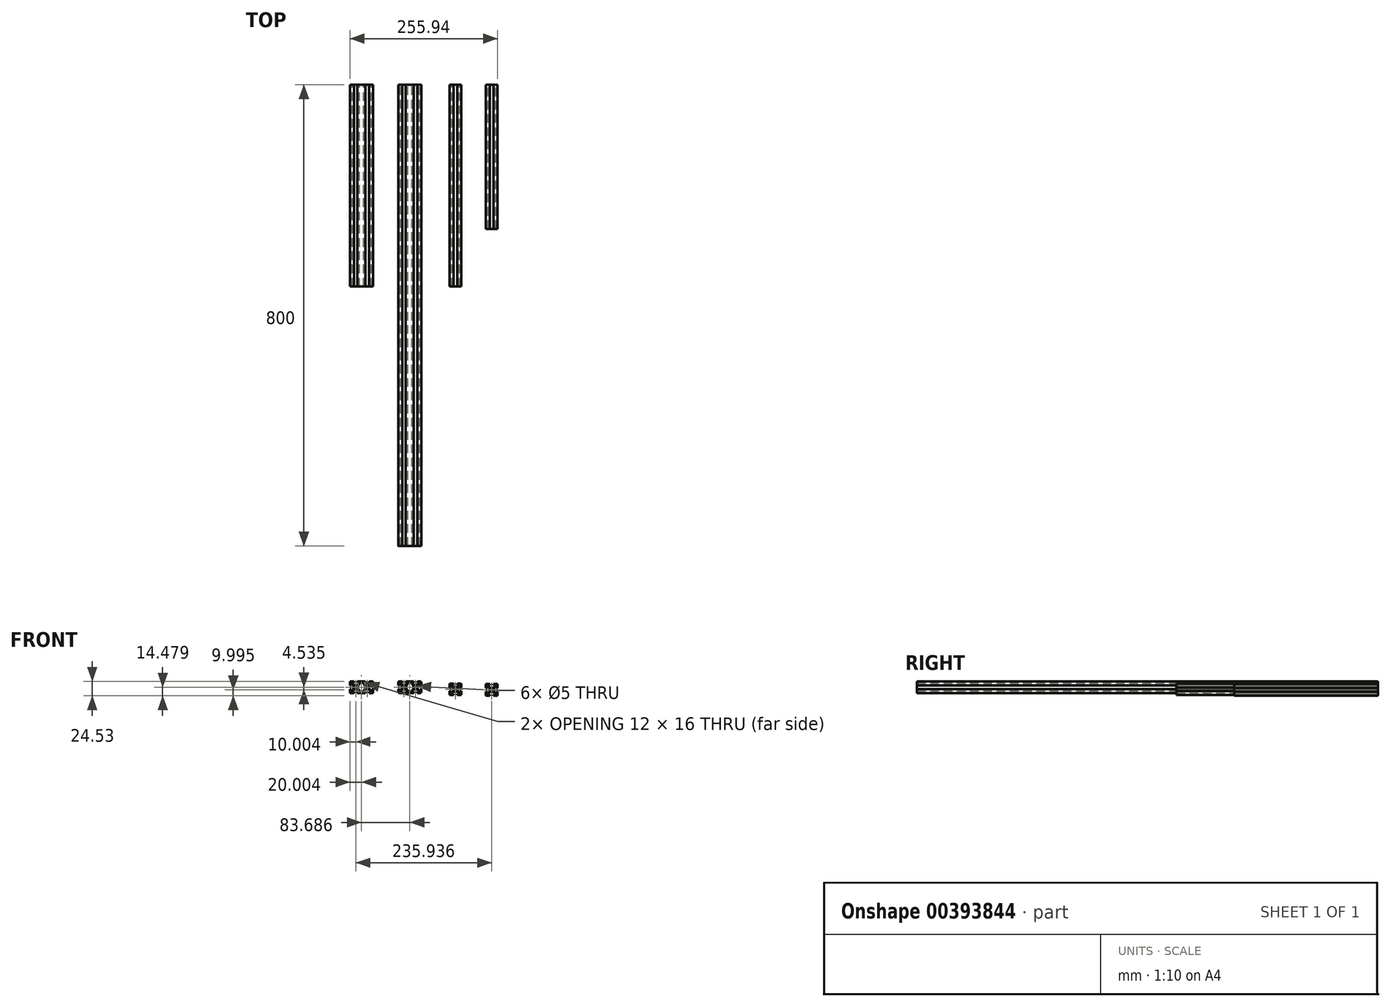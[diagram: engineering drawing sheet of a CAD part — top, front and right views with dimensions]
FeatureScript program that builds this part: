
annotation { "Feature Type Name" : "Feature", "Feature Type Description" : "" }
export const myFeature = defineFeature(function(context is Context, id is Id, definition is map)
    precondition{}
    {
        {
            var Q0;
            Q0=qCreatedBy(makeId("Front.planeOp"),FACE);
            var sketch = newSketch(context, id + "F0", { "sketchPlane" : qUnion([Q0])});
            skLineSegment(sketch, "E0.bottom", {"start": v(-20, 10) * mm, "end": v(-13, 10) * mm});
            skLineSegment(sketch, "E0.top", {"start": v(-20, -10) * mm, "end": v(-13, -10) * mm});
            skLineSegment(sketch, "E0.left", {"start": v(-20, 10) * mm, "end": v(-20, 3) * mm});
            skPoint(sketch, "E1.endSnap0", {"position": v(0, -10) * mm});
            skLineSegment(sketch, "E2", {"start": v(-26.6, 0) * mm, "end": v(32.73, 0) * mm, "construction": true});
            skCircle(sketch, "E3", {"center": v(10, 0) * mm, "radius": 2.5 * mm});
            skCircle(sketch, "E4", {"center": v(-10, 0) * mm, "radius": 2.5 * mm});
            skLineSegment(sketch, "E5", {"start": v(4.5, 8) * mm, "end": v(7, 8) * mm});
            skLineSegment(sketch, "E6", {"start": v(15.5, 8) * mm, "end": v(15.5, 6.5) * mm});
            skLineSegment(sketch, "E7", {"start": v(15.5, 6.5) * mm, "end": v(13, 4) * mm});
            skLineSegment(sketch, "E8", {"start": v(13, 4) * mm, "end": v(7, 4) * mm});
            skLineSegment(sketch, "E9", {"start": v(7, 4) * mm, "end": v(4.5, 6.5) * mm});
            skLineSegment(sketch, "E10", {"start": v(4.5, 6.5) * mm, "end": v(4.5, 8) * mm});
            skLineSegment(sketch, "E11", {"start": v(0, 29.93) * mm, "end": v(0, -23.02) * mm, "construction": true});
            skLineSegment(sketch, "E12", {"start": v(7, 8) * mm, "end": v(7, 10) * mm});
            skLineSegment(sketch, "E13", {"start": v(13, 8) * mm, "end": v(13, 10) * mm});
            skLineSegment(sketch, "E14.trimOffspring", {"start": v(13, 8) * mm, "end": v(15.5, 8) * mm});
            skLineSegment(sketch, "E15.trimOffspring", {"start": v(13, 10) * mm, "end": v(20, 10) * mm});
            skLineSegment(sketch, "E16.1.3", {"start": v(6, -3) * mm, "end": v(3.5, -5.5) * mm});
            skLineSegment(sketch, "E16.1.4", {"start": v(6, 3) * mm, "end": v(6, -3) * mm});
            skLineSegment(sketch, "E16.1.5", {"start": v(3.5, 5.5) * mm, "end": v(6, 3) * mm});
            skLineSegment(sketch, "E16.2.0", {"start": v(13, -8) * mm, "end": v(13, -10) * mm});
            skLineSegment(sketch, "E16.2.1", {"start": v(15.5, -8) * mm, "end": v(13, -8) * mm});
            skLineSegment(sketch, "E16.2.2", {"start": v(15.5, -6.5) * mm, "end": v(15.5, -8) * mm});
            skLineSegment(sketch, "E16.2.3", {"start": v(13, -4) * mm, "end": v(15.5, -6.5) * mm});
            skLineSegment(sketch, "E16.2.4", {"start": v(7, -4) * mm, "end": v(13, -4) * mm});
            skLineSegment(sketch, "E16.2.5", {"start": v(4.5, -6.5) * mm, "end": v(7, -4) * mm});
            skLineSegment(sketch, "E16.2.6", {"start": v(7, -8) * mm, "end": v(7, -10) * mm});
            skLineSegment(sketch, "E16.2.7", {"start": v(7, -8) * mm, "end": v(4.5, -8) * mm});
            skLineSegment(sketch, "E16.2.8", {"start": v(4.5, -8) * mm, "end": v(4.5, -6.5) * mm});
            skLineSegment(sketch, "E16.3.0", {"start": v(18, 3) * mm, "end": v(20, 3) * mm});
            skLineSegment(sketch, "E16.3.1", {"start": v(18, 5.5) * mm, "end": v(18, 3) * mm});
            skLineSegment(sketch, "E16.3.2", {"start": v(16.5, 5.5) * mm, "end": v(18, 5.5) * mm});
            skLineSegment(sketch, "E16.3.3", {"start": v(14, 3) * mm, "end": v(16.5, 5.5) * mm});
            skLineSegment(sketch, "E16.3.4", {"start": v(14, -3) * mm, "end": v(14, 3) * mm});
            skLineSegment(sketch, "E16.3.5", {"start": v(16.5, -5.5) * mm, "end": v(14, -3) * mm});
            skLineSegment(sketch, "E16.3.6", {"start": v(18, -3) * mm, "end": v(20, -3) * mm});
            skLineSegment(sketch, "E16.3.7", {"start": v(18, -3) * mm, "end": v(18, -5.5) * mm});
            skLineSegment(sketch, "E16.3.8", {"start": v(18, -5.5) * mm, "end": v(16.5, -5.5) * mm});
            skLineSegment(sketch, "E17.MirrorCS", {"start": v(-4.5, -8) * mm, "end": v(-4.5, -6.5) * mm});
            skLineSegment(sketch, "E18.MirrorCS", {"start": v(-4.5, -6.5) * mm, "end": v(-7, -4) * mm});
            skLineSegment(sketch, "E19.MirrorCS", {"start": v(-7, -4) * mm, "end": v(-13, -4) * mm});
            skLineSegment(sketch, "E20.MirrorCS", {"start": v(-7, -8) * mm, "end": v(-4.5, -8) * mm});
            skLineSegment(sketch, "E21.MirrorCS", {"start": v(-7, -8) * mm, "end": v(-7, -10) * mm});
            skLineSegment(sketch, "E22.MirrorCS", {"start": v(-13, -8) * mm, "end": v(-13, -10) * mm});
            skLineSegment(sketch, "E23.MirrorCS", {"start": v(-15.5, -8) * mm, "end": v(-13, -8) * mm});
            skLineSegment(sketch, "E24.MirrorCS", {"start": v(-15.5, -6.5) * mm, "end": v(-15.5, -8) * mm});
            skLineSegment(sketch, "E25.MirrorCS", {"start": v(-13, -4) * mm, "end": v(-15.5, -6.5) * mm});
            skLineSegment(sketch, "E26.MirrorCS", {"start": v(-14, -3) * mm, "end": v(-14, 3) * mm});
            skLineSegment(sketch, "E27.MirrorCS", {"start": v(-16.5, -5.5) * mm, "end": v(-14, -3) * mm});
            skLineSegment(sketch, "E28.MirrorCS", {"start": v(-18, -5.5) * mm, "end": v(-16.5, -5.5) * mm});
            skLineSegment(sketch, "E29.MirrorCS", {"start": v(-18, -3) * mm, "end": v(-18, -5.5) * mm});
            skLineSegment(sketch, "E30.MirrorCS", {"start": v(-18, -3) * mm, "end": v(-20, -3) * mm});
            skLineSegment(sketch, "E31.MirrorCS", {"start": v(-18, 3) * mm, "end": v(-20, 3) * mm});
            skLineSegment(sketch, "E32.MirrorCS", {"start": v(-16.5, 5.5) * mm, "end": v(-18, 5.5) * mm});
            skLineSegment(sketch, "E33.MirrorCS", {"start": v(-14, 3) * mm, "end": v(-16.5, 5.5) * mm});
            skLineSegment(sketch, "E34.MirrorCS", {"start": v(-18, 5.5) * mm, "end": v(-18, 3) * mm});
            skLineSegment(sketch, "E35.MirrorCS", {"start": v(-7, 8) * mm, "end": v(-7, 10) * mm});
            skLineSegment(sketch, "E36.MirrorCS", {"start": v(-4.5, 8) * mm, "end": v(-7, 8) * mm});
            skLineSegment(sketch, "E37.MirrorCS", {"start": v(-4.5, 6.5) * mm, "end": v(-4.5, 8) * mm});
            skLineSegment(sketch, "E38.MirrorCS", {"start": v(-7, 4) * mm, "end": v(-4.5, 6.5) * mm});
            skLineSegment(sketch, "E39.MirrorCS", {"start": v(-13, 4) * mm, "end": v(-7, 4) * mm});
            skLineSegment(sketch, "E40.MirrorCS", {"start": v(-15.5, 6.5) * mm, "end": v(-13, 4) * mm});
            skLineSegment(sketch, "E41.MirrorCS", {"start": v(-15.5, 8) * mm, "end": v(-15.5, 6.5) * mm});
            skLineSegment(sketch, "E42.MirrorCS", {"start": v(-13, 8) * mm, "end": v(-15.5, 8) * mm});
            skLineSegment(sketch, "E43.MirrorCS", {"start": v(-13, 8) * mm, "end": v(-13, 10) * mm});
            skLineSegment(sketch, "E44.MirrorCS", {"start": v(-3.5, 5.5) * mm, "end": v(-6, 3) * mm});
            skLineSegment(sketch, "E45.MirrorCS", {"start": v(-6, 3) * mm, "end": v(-6, -3) * mm});
            skLineSegment(sketch, "E46.MirrorCS", {"start": v(-6, -3) * mm, "end": v(-3.5, -5.5) * mm});
            skLineSegment(sketch, "E47", {"start": v(-3.5, 5.5) * mm, "end": v(-3.5, 8) * mm});
            skLineSegment(sketch, "E48", {"start": v(3.5, 5.5) * mm, "end": v(3.5, 8) * mm});
            skLineSegment(sketch, "E49", {"start": v(3.5, 8) * mm, "end": v(-3.5, 8) * mm});
            skLineSegment(sketch, "E50.trimOffspring", {"start": v(-20, -3) * mm, "end": v(-20, -10) * mm});
            skLineSegment(sketch, "E51.trimOffspring", {"start": v(-7, 10) * mm, "end": v(7, 10) * mm});
            skLineSegment(sketch, "E52.trimOffspring", {"start": v(20, -3) * mm, "end": v(20, -10) * mm});
            skLineSegment(sketch, "E53.trimOffspring", {"start": v(13, -10) * mm, "end": v(20, -10) * mm});
            skLineSegment(sketch, "E54.trimOffspring", {"start": v(-7, -10) * mm, "end": v(7, -10) * mm});
            skLineSegment(sketch, "E55.MirrorCS", {"start": v(-3.5, -5.5) * mm, "end": v(-3.5, -8) * mm});
            skLineSegment(sketch, "E56.MirrorCS", {"start": v(3.5, -8) * mm, "end": v(-3.5, -8) * mm});
            skLineSegment(sketch, "E57.MirrorCS", {"start": v(3.5, -5.5) * mm, "end": v(3.5, -8) * mm});
            skLineSegment(sketch, "E58", {"start": v(20, 10) * mm, "end": v(20, 3) * mm});
            skSolve(sketch);
        }
        {
            var Q0;
            Q0=qSketchRegion(id+"F0",true);
            extrude(context, id + "F1", {"entities" : qUnion([Q0]), "depth" : 800 * mm});
        }
        {
            var Q0;
            Q0=makeQuery(id+"F1.opExtrude","SWEPT_EDGE",EDGE,{"disambiguationData":[OSD([sQuery(id+"F0.wireOp",EDGE,"E15.trimOffspring"),sQuery(id+"F0.wireOp",EDGE,"E58")])]});
            var Q1;
            Q1=makeQuery(id+"F1.opExtrude","SWEPT_EDGE",EDGE,{"disambiguationData":[OSD([sQuery(id+"F0.wireOp",EDGE,"E0.bottom"),sQuery(id+"F0.wireOp",EDGE,"E0.left")])]});
            var Q2;
            Q2=makeQuery(id+"F1.opExtrude","SWEPT_EDGE",EDGE,{"disambiguationData":[OSD([sQuery(id+"F0.wireOp",EDGE,"E0.top"),sQuery(id+"F0.wireOp",EDGE,"E50.trimOffspring")])]});
            var Q3;
            Q3=makeQuery(id+"F1.opExtrude","SWEPT_EDGE",EDGE,{"disambiguationData":[OSD([sQuery(id+"F0.wireOp",EDGE,"E52.trimOffspring"),sQuery(id+"F0.wireOp",EDGE,"E53.trimOffspring")])]});
            fillet(context, id + "F2", {"entities" : qUnion([Q0, Q1, Q2, Q3]), "radius" : 2 * mm, "tangentPropagation" : true, "allowEdgeOverflow" : false});
        }
        {
            var Q0;
            Q0=qCreatedBy(makeId("Front.planeOp"),FACE);
            var sketch = newSketch(context, id + "F3", { "sketchPlane" : qUnion([Q0])});
            skLineSegment(sketch, "E59.bottom", {"start": v(-103.69, 9.95) * mm, "end": v(-96.69, 9.95) * mm});
            skLineSegment(sketch, "E59.top", {"start": v(-103.69, -10.05) * mm, "end": v(-96.69, -10.05) * mm});
            skLineSegment(sketch, "E59.left", {"start": v(-103.69, 9.95) * mm, "end": v(-103.69, 2.95) * mm});
            skPoint(sketch, "E60.endSnap0", {"position": v(-83.69, -10.05) * mm});
            skLineSegment(sketch, "E61", {"start": v(-110.28, -0.05) * mm, "end": v(-50.95, -0.05) * mm, "construction": true});
            skCircle(sketch, "E62", {"center": v(-73.69, -0.05) * mm, "radius": 2.5 * mm});
            skCircle(sketch, "E63", {"center": v(-93.69, -0.05) * mm, "radius": 2.5 * mm});
            skLineSegment(sketch, "E64", {"start": v(-79.19, 7.95) * mm, "end": v(-76.69, 7.95) * mm});
            skLineSegment(sketch, "E65", {"start": v(-68.19, 7.95) * mm, "end": v(-68.19, 6.45) * mm});
            skLineSegment(sketch, "E66", {"start": v(-68.19, 6.45) * mm, "end": v(-70.69, 3.95) * mm});
            skLineSegment(sketch, "E67", {"start": v(-70.69, 3.95) * mm, "end": v(-76.69, 3.95) * mm});
            skLineSegment(sketch, "E68", {"start": v(-76.69, 3.95) * mm, "end": v(-79.19, 6.45) * mm});
            skLineSegment(sketch, "E69", {"start": v(-79.19, 6.45) * mm, "end": v(-79.19, 7.95) * mm});
            skLineSegment(sketch, "E70", {"start": v(-83.69, 29.88) * mm, "end": v(-83.69, -23.07) * mm, "construction": true});
            skLineSegment(sketch, "E71", {"start": v(-76.69, 7.95) * mm, "end": v(-76.69, 9.95) * mm});
            skLineSegment(sketch, "E72", {"start": v(-70.69, 7.95) * mm, "end": v(-70.69, 9.95) * mm});
            skLineSegment(sketch, "E73.trimOffspring", {"start": v(-70.69, 7.95) * mm, "end": v(-68.19, 7.95) * mm});
            skLineSegment(sketch, "E74.trimOffspring", {"start": v(-70.69, 9.95) * mm, "end": v(-63.69, 9.95) * mm});
            skLineSegment(sketch, "E75.1.3", {"start": v(-77.69, -3.05) * mm, "end": v(-80.19, -5.55) * mm});
            skLineSegment(sketch, "E75.1.4", {"start": v(-77.69, 2.95) * mm, "end": v(-77.69, -3.05) * mm});
            skLineSegment(sketch, "E75.1.5", {"start": v(-80.19, 5.45) * mm, "end": v(-77.69, 2.95) * mm});
            skLineSegment(sketch, "E75.2.0", {"start": v(-70.69, -8.05) * mm, "end": v(-70.69, -10.05) * mm});
            skLineSegment(sketch, "E75.2.1", {"start": v(-68.19, -8.05) * mm, "end": v(-70.69, -8.05) * mm});
            skLineSegment(sketch, "E75.2.2", {"start": v(-68.19, -6.55) * mm, "end": v(-68.19, -8.05) * mm});
            skLineSegment(sketch, "E75.2.3", {"start": v(-70.69, -4.05) * mm, "end": v(-68.19, -6.55) * mm});
            skLineSegment(sketch, "E75.2.4", {"start": v(-76.69, -4.05) * mm, "end": v(-70.69, -4.05) * mm});
            skLineSegment(sketch, "E75.2.5", {"start": v(-79.19, -6.55) * mm, "end": v(-76.69, -4.05) * mm});
            skLineSegment(sketch, "E75.2.6", {"start": v(-76.69, -8.05) * mm, "end": v(-76.69, -10.05) * mm});
            skLineSegment(sketch, "E75.2.7", {"start": v(-76.69, -8.05) * mm, "end": v(-79.19, -8.05) * mm});
            skLineSegment(sketch, "E75.2.8", {"start": v(-79.19, -8.05) * mm, "end": v(-79.19, -6.55) * mm});
            skLineSegment(sketch, "E75.3.0", {"start": v(-65.69, 2.95) * mm, "end": v(-63.69, 2.95) * mm});
            skLineSegment(sketch, "E75.3.1", {"start": v(-65.69, 5.45) * mm, "end": v(-65.69, 2.95) * mm});
            skLineSegment(sketch, "E75.3.2", {"start": v(-67.19, 5.45) * mm, "end": v(-65.69, 5.45) * mm});
            skLineSegment(sketch, "E75.3.3", {"start": v(-69.69, 2.95) * mm, "end": v(-67.19, 5.45) * mm});
            skLineSegment(sketch, "E75.3.4", {"start": v(-69.69, -3.05) * mm, "end": v(-69.69, 2.95) * mm});
            skLineSegment(sketch, "E75.3.5", {"start": v(-67.19, -5.55) * mm, "end": v(-69.69, -3.05) * mm});
            skLineSegment(sketch, "E75.3.6", {"start": v(-65.69, -3.05) * mm, "end": v(-63.69, -3.05) * mm});
            skLineSegment(sketch, "E75.3.7", {"start": v(-65.69, -3.05) * mm, "end": v(-65.69, -5.55) * mm});
            skLineSegment(sketch, "E75.3.8", {"start": v(-65.69, -5.55) * mm, "end": v(-67.19, -5.55) * mm});
            skLineSegment(sketch, "E76.MirrorCS", {"start": v(-88.19, -8.05) * mm, "end": v(-88.19, -6.55) * mm});
            skLineSegment(sketch, "E77.MirrorCS", {"start": v(-88.19, -6.55) * mm, "end": v(-90.69, -4.05) * mm});
            skLineSegment(sketch, "E78.MirrorCS", {"start": v(-90.69, -4.05) * mm, "end": v(-96.69, -4.05) * mm});
            skLineSegment(sketch, "E79.MirrorCS", {"start": v(-90.69, -8.05) * mm, "end": v(-88.19, -8.05) * mm});
            skLineSegment(sketch, "E80.MirrorCS", {"start": v(-90.69, -8.05) * mm, "end": v(-90.69, -10.05) * mm});
            skLineSegment(sketch, "E81.MirrorCS", {"start": v(-96.69, -8.05) * mm, "end": v(-96.69, -10.05) * mm});
            skLineSegment(sketch, "E82.MirrorCS", {"start": v(-99.19, -8.05) * mm, "end": v(-96.69, -8.05) * mm});
            skLineSegment(sketch, "E83.MirrorCS", {"start": v(-99.19, -6.55) * mm, "end": v(-99.19, -8.05) * mm});
            skLineSegment(sketch, "E84.MirrorCS", {"start": v(-96.69, -4.05) * mm, "end": v(-99.19, -6.55) * mm});
            skLineSegment(sketch, "E85.MirrorCS", {"start": v(-97.69, -3.05) * mm, "end": v(-97.69, 2.95) * mm});
            skLineSegment(sketch, "E86.MirrorCS", {"start": v(-100.19, -5.55) * mm, "end": v(-97.69, -3.05) * mm});
            skLineSegment(sketch, "E87.MirrorCS", {"start": v(-101.69, -5.55) * mm, "end": v(-100.19, -5.55) * mm});
            skLineSegment(sketch, "E88.MirrorCS", {"start": v(-101.69, -3.05) * mm, "end": v(-101.69, -5.55) * mm});
            skLineSegment(sketch, "E89.MirrorCS", {"start": v(-101.69, -3.05) * mm, "end": v(-103.69, -3.05) * mm});
            skLineSegment(sketch, "E90.MirrorCS", {"start": v(-101.69, 2.95) * mm, "end": v(-103.69, 2.95) * mm});
            skLineSegment(sketch, "E91.MirrorCS", {"start": v(-100.19, 5.45) * mm, "end": v(-101.69, 5.45) * mm});
            skLineSegment(sketch, "E92.MirrorCS", {"start": v(-97.69, 2.95) * mm, "end": v(-100.19, 5.45) * mm});
            skLineSegment(sketch, "E93.MirrorCS", {"start": v(-101.69, 5.45) * mm, "end": v(-101.69, 2.95) * mm});
            skLineSegment(sketch, "E94.MirrorCS", {"start": v(-90.69, 7.95) * mm, "end": v(-90.69, 9.95) * mm});
            skLineSegment(sketch, "E95.MirrorCS", {"start": v(-88.19, 7.95) * mm, "end": v(-90.69, 7.95) * mm});
            skLineSegment(sketch, "E96.MirrorCS", {"start": v(-88.19, 6.45) * mm, "end": v(-88.19, 7.95) * mm});
            skLineSegment(sketch, "E97.MirrorCS", {"start": v(-90.69, 3.95) * mm, "end": v(-88.19, 6.45) * mm});
            skLineSegment(sketch, "E98.MirrorCS", {"start": v(-96.69, 3.95) * mm, "end": v(-90.69, 3.95) * mm});
            skLineSegment(sketch, "E99.MirrorCS", {"start": v(-99.19, 6.45) * mm, "end": v(-96.69, 3.95) * mm});
            skLineSegment(sketch, "E100.MirrorCS", {"start": v(-99.19, 7.95) * mm, "end": v(-99.19, 6.45) * mm});
            skLineSegment(sketch, "E101.MirrorCS", {"start": v(-96.69, 7.95) * mm, "end": v(-99.19, 7.95) * mm});
            skLineSegment(sketch, "E102.MirrorCS", {"start": v(-96.69, 7.95) * mm, "end": v(-96.69, 9.95) * mm});
            skLineSegment(sketch, "E103.MirrorCS", {"start": v(-87.19, 5.45) * mm, "end": v(-89.69, 2.95) * mm});
            skLineSegment(sketch, "E104.MirrorCS", {"start": v(-89.69, 2.95) * mm, "end": v(-89.69, -3.05) * mm});
            skLineSegment(sketch, "E105.MirrorCS", {"start": v(-89.69, -3.05) * mm, "end": v(-87.19, -5.55) * mm});
            skLineSegment(sketch, "E106", {"start": v(-87.19, 5.45) * mm, "end": v(-87.19, 7.95) * mm});
            skLineSegment(sketch, "E107", {"start": v(-80.19, 5.45) * mm, "end": v(-80.19, 7.95) * mm});
            skLineSegment(sketch, "E108", {"start": v(-80.19, 7.95) * mm, "end": v(-87.19, 7.95) * mm});
            skLineSegment(sketch, "E109.trimOffspring", {"start": v(-103.69, -3.05) * mm, "end": v(-103.69, -10.05) * mm});
            skLineSegment(sketch, "E110.trimOffspring", {"start": v(-90.69, 9.95) * mm, "end": v(-76.69, 9.95) * mm});
            skLineSegment(sketch, "E111.trimOffspring", {"start": v(-63.69, -3.05) * mm, "end": v(-63.69, -10.05) * mm});
            skLineSegment(sketch, "E112.trimOffspring", {"start": v(-70.69, -10.05) * mm, "end": v(-63.69, -10.05) * mm});
            skLineSegment(sketch, "E113.trimOffspring", {"start": v(-90.69, -10.05) * mm, "end": v(-76.69, -10.05) * mm});
            skLineSegment(sketch, "E114.MirrorCS", {"start": v(-87.19, -5.55) * mm, "end": v(-87.19, -8.05) * mm});
            skLineSegment(sketch, "E115.MirrorCS", {"start": v(-80.19, -8.05) * mm, "end": v(-87.19, -8.05) * mm});
            skLineSegment(sketch, "E116.MirrorCS", {"start": v(-80.19, -5.55) * mm, "end": v(-80.19, -8.05) * mm});
            skLineSegment(sketch, "E117", {"start": v(-63.69, 9.95) * mm, "end": v(-63.69, 2.95) * mm});
            skSolve(sketch);
        }
        {
            var Q0;
            Q0=qSketchRegion(id+"F3",true);
            extrude(context, id + "F4", {"entities" : qUnion([Q0]), "depth" : 350 * mm});
        }
        {
            var Q0;
            Q0=qCreatedBy(makeId("Front.planeOp"),FACE);
            var sketch = newSketch(context, id + "F5", { "sketchPlane" : qUnion([Q0])});
            skPoint(sketch, "E118.endSnap0", {"position": v(69.36, -13.62) * mm});
            skLineSegment(sketch, "E119", {"start": v(42.77, -3.62) * mm, "end": v(102.1, -3.62) * mm, "construction": true});
            skCircle(sketch, "E120", {"center": v(79.36, -3.62) * mm, "radius": 2.5 * mm});
            skLineSegment(sketch, "E121", {"start": v(84.86, 4.37) * mm, "end": v(84.86, 2.87) * mm});
            skLineSegment(sketch, "E122", {"start": v(84.86, 2.87) * mm, "end": v(82.36, 0.37) * mm});
            skLineSegment(sketch, "E123", {"start": v(82.36, 0.37) * mm, "end": v(76.36, 0.37) * mm});
            skLineSegment(sketch, "E124", {"start": v(76.36, 0.37) * mm, "end": v(73.86, 2.87) * mm});
            skLineSegment(sketch, "E125", {"start": v(73.86, 2.87) * mm, "end": v(73.86, 4.37) * mm});
            skLineSegment(sketch, "E126", {"start": v(76.36, 4.37) * mm, "end": v(76.36, 6.38) * mm});
            skLineSegment(sketch, "E127", {"start": v(82.36, 4.37) * mm, "end": v(82.36, 6.38) * mm});
            skLineSegment(sketch, "E128.trimOffspring", {"start": v(82.36, 4.37) * mm, "end": v(84.86, 4.37) * mm});
            skLineSegment(sketch, "E129.trimOffspring", {"start": v(82.36, 6.38) * mm, "end": v(89.36, 6.38) * mm});
            skLineSegment(sketch, "E130.1.3", {"start": v(75.36, -6.62) * mm, "end": v(72.86, -9.12) * mm});
            skLineSegment(sketch, "E130.1.4", {"start": v(75.36, -0.62) * mm, "end": v(75.36, -6.62) * mm});
            skLineSegment(sketch, "E130.1.5", {"start": v(72.86, 1.88) * mm, "end": v(75.36, -0.62) * mm});
            skLineSegment(sketch, "E130.2.0", {"start": v(82.36, -11.62) * mm, "end": v(82.36, -13.62) * mm});
            skLineSegment(sketch, "E130.2.1", {"start": v(84.86, -11.62) * mm, "end": v(82.36, -11.62) * mm});
            skLineSegment(sketch, "E130.2.2", {"start": v(84.86, -10.12) * mm, "end": v(84.86, -11.62) * mm});
            skLineSegment(sketch, "E130.2.3", {"start": v(82.36, -7.62) * mm, "end": v(84.86, -10.12) * mm});
            skLineSegment(sketch, "E130.2.4", {"start": v(76.36, -7.62) * mm, "end": v(82.36, -7.62) * mm});
            skLineSegment(sketch, "E130.2.5", {"start": v(73.86, -10.12) * mm, "end": v(76.36, -7.62) * mm});
            skLineSegment(sketch, "E130.2.6", {"start": v(76.36, -11.62) * mm, "end": v(76.36, -13.62) * mm});
            skLineSegment(sketch, "E130.2.7", {"start": v(76.36, -11.62) * mm, "end": v(73.86, -11.62) * mm});
            skLineSegment(sketch, "E130.2.8", {"start": v(73.86, -11.62) * mm, "end": v(73.86, -10.12) * mm});
            skLineSegment(sketch, "E130.3.0", {"start": v(87.36, -0.62) * mm, "end": v(89.36, -0.62) * mm});
            skLineSegment(sketch, "E130.3.1", {"start": v(87.36, 1.88) * mm, "end": v(87.36, -0.62) * mm});
            skLineSegment(sketch, "E130.3.2", {"start": v(85.86, 1.88) * mm, "end": v(87.36, 1.88) * mm});
            skLineSegment(sketch, "E130.3.3", {"start": v(83.36, -0.62) * mm, "end": v(85.86, 1.88) * mm});
            skLineSegment(sketch, "E130.3.4", {"start": v(83.36, -6.62) * mm, "end": v(83.36, -0.62) * mm});
            skLineSegment(sketch, "E130.3.5", {"start": v(85.86, -9.12) * mm, "end": v(83.36, -6.62) * mm});
            skLineSegment(sketch, "E130.3.6", {"start": v(87.36, -6.62) * mm, "end": v(89.36, -6.62) * mm});
            skLineSegment(sketch, "E130.3.7", {"start": v(87.36, -6.62) * mm, "end": v(87.36, -9.12) * mm});
            skLineSegment(sketch, "E130.3.8", {"start": v(87.36, -9.12) * mm, "end": v(85.86, -9.12) * mm});
            skLineSegment(sketch, "E131.trimOffspring", {"start": v(69.36, 6.38) * mm, "end": v(76.36, 6.38) * mm});
            skLineSegment(sketch, "E132.trimOffspring", {"start": v(89.36, -6.62) * mm, "end": v(89.36, -13.62) * mm});
            skLineSegment(sketch, "E133.trimOffspring", {"start": v(82.36, -13.62) * mm, "end": v(89.36, -13.62) * mm});
            skLineSegment(sketch, "E134.trimOffspring", {"start": v(69.36, -13.62) * mm, "end": v(76.36, -13.62) * mm});
            skLineSegment(sketch, "E135", {"start": v(89.36, 6.38) * mm, "end": v(89.36, -0.62) * mm});
            skLineSegment(sketch, "E136", {"start": v(79.36, -3.62) * mm, "end": v(79.36, -16.55) * mm, "construction": true});
            skLineSegment(sketch, "E137.MirrorCS", {"start": v(69.36, -6.62) * mm, "end": v(69.36, -13.62) * mm});
            skLineSegment(sketch, "E138.MirrorCS", {"start": v(71.36, -9.12) * mm, "end": v(72.86, -9.12) * mm});
            skLineSegment(sketch, "E139.MirrorCS", {"start": v(71.36, -6.62) * mm, "end": v(71.36, -9.12) * mm});
            skLineSegment(sketch, "E140.MirrorCS", {"start": v(76.36, 4.37) * mm, "end": v(73.86, 4.37) * mm});
            skLineSegment(sketch, "E141.MirrorCS", {"start": v(69.36, 6.38) * mm, "end": v(69.36, -0.62) * mm});
            skLineSegment(sketch, "E142.MirrorCS", {"start": v(71.36, 1.88) * mm, "end": v(71.36, -0.62) * mm});
            skLineSegment(sketch, "E143.MirrorCS", {"start": v(71.36, -0.62) * mm, "end": v(69.36, -0.62) * mm});
            skLineSegment(sketch, "E144.MirrorCS", {"start": v(72.86, 1.88) * mm, "end": v(71.36, 1.88) * mm});
            skLineSegment(sketch, "E145", {"start": v(69.36, -6.62) * mm, "end": v(71.36, -6.62) * mm});
            skSolve(sketch);
        }
        {
            var Q0;
            Q0=qSketchRegion(id+"F5",true);
            extrude(context, id + "F6", {"entities" : qUnion([Q0]), "depth" : 350 * mm});
        }
        {
            var Q0;
            Q0=qCreatedBy(makeId("Front.planeOp"),FACE);
            var sketch = newSketch(context, id + "F7", { "sketchPlane" : qUnion([Q0])});
            skPoint(sketch, "E146.endSnap0", {"position": v(132.25, -14.53) * mm});
            skCircle(sketch, "E147", {"center": v(142.25, -4.53) * mm, "radius": 2.5 * mm});
            skLineSegment(sketch, "E148", {"start": v(147.75, 3.46) * mm, "end": v(147.75, 1.96) * mm});
            skLineSegment(sketch, "E149", {"start": v(147.75, 1.96) * mm, "end": v(145.25, -0.54) * mm});
            skLineSegment(sketch, "E150", {"start": v(145.25, -0.54) * mm, "end": v(139.25, -0.54) * mm});
            skLineSegment(sketch, "E151", {"start": v(139.25, -0.54) * mm, "end": v(136.75, 1.96) * mm});
            skLineSegment(sketch, "E152", {"start": v(136.75, 1.96) * mm, "end": v(136.75, 3.46) * mm});
            skLineSegment(sketch, "E153", {"start": v(139.25, 3.46) * mm, "end": v(139.25, 5.47) * mm});
            skLineSegment(sketch, "E154", {"start": v(145.25, 3.46) * mm, "end": v(145.25, 5.47) * mm});
            skLineSegment(sketch, "E155.trimOffspring", {"start": v(145.25, 3.46) * mm, "end": v(147.75, 3.46) * mm});
            skLineSegment(sketch, "E156.trimOffspring", {"start": v(145.25, 5.47) * mm, "end": v(152.25, 5.47) * mm});
            skLineSegment(sketch, "E157.1.3", {"start": v(138.25, -7.53) * mm, "end": v(135.75, -10.03) * mm});
            skLineSegment(sketch, "E157.1.4", {"start": v(138.25, -1.53) * mm, "end": v(138.25, -7.53) * mm});
            skLineSegment(sketch, "E157.1.5", {"start": v(135.75, 0.97) * mm, "end": v(138.25, -1.53) * mm});
            skLineSegment(sketch, "E157.2.0", {"start": v(145.25, -12.53) * mm, "end": v(145.25, -14.53) * mm});
            skLineSegment(sketch, "E157.2.1", {"start": v(147.75, -12.53) * mm, "end": v(145.25, -12.53) * mm});
            skLineSegment(sketch, "E157.2.2", {"start": v(147.75, -11.03) * mm, "end": v(147.75, -12.53) * mm});
            skLineSegment(sketch, "E157.2.3", {"start": v(145.25, -8.53) * mm, "end": v(147.75, -11.03) * mm});
            skLineSegment(sketch, "E157.2.4", {"start": v(139.25, -8.53) * mm, "end": v(145.25, -8.53) * mm});
            skLineSegment(sketch, "E157.2.5", {"start": v(136.75, -11.03) * mm, "end": v(139.25, -8.53) * mm});
            skLineSegment(sketch, "E157.2.6", {"start": v(139.25, -12.53) * mm, "end": v(139.25, -14.53) * mm});
            skLineSegment(sketch, "E157.2.7", {"start": v(139.25, -12.53) * mm, "end": v(136.75, -12.53) * mm});
            skLineSegment(sketch, "E157.2.8", {"start": v(136.75, -12.53) * mm, "end": v(136.75, -11.03) * mm});
            skLineSegment(sketch, "E157.3.0", {"start": v(150.25, -1.53) * mm, "end": v(152.25, -1.53) * mm});
            skLineSegment(sketch, "E157.3.1", {"start": v(150.25, 0.97) * mm, "end": v(150.25, -1.53) * mm});
            skLineSegment(sketch, "E157.3.2", {"start": v(148.75, 0.97) * mm, "end": v(150.25, 0.97) * mm});
            skLineSegment(sketch, "E157.3.3", {"start": v(146.25, -1.53) * mm, "end": v(148.75, 0.97) * mm});
            skLineSegment(sketch, "E157.3.4", {"start": v(146.25, -7.53) * mm, "end": v(146.25, -1.53) * mm});
            skLineSegment(sketch, "E157.3.5", {"start": v(148.75, -10.03) * mm, "end": v(146.25, -7.53) * mm});
            skLineSegment(sketch, "E157.3.6", {"start": v(150.25, -7.53) * mm, "end": v(152.25, -7.53) * mm});
            skLineSegment(sketch, "E157.3.7", {"start": v(150.25, -7.53) * mm, "end": v(150.25, -10.03) * mm});
            skLineSegment(sketch, "E157.3.8", {"start": v(150.25, -10.03) * mm, "end": v(148.75, -10.03) * mm});
            skLineSegment(sketch, "E158.trimOffspring", {"start": v(132.25, 5.47) * mm, "end": v(139.25, 5.47) * mm});
            skLineSegment(sketch, "E159.trimOffspring", {"start": v(152.25, -7.53) * mm, "end": v(152.25, -14.53) * mm});
            skLineSegment(sketch, "E160.trimOffspring", {"start": v(145.25, -14.53) * mm, "end": v(152.25, -14.53) * mm});
            skLineSegment(sketch, "E161.trimOffspring", {"start": v(132.25, -14.53) * mm, "end": v(139.25, -14.53) * mm});
            skLineSegment(sketch, "E162", {"start": v(152.25, 5.47) * mm, "end": v(152.25, -1.53) * mm});
            skLineSegment(sketch, "E163", {"start": v(142.25, -4.53) * mm, "end": v(142.25, -17.46) * mm, "construction": true});
            skLineSegment(sketch, "E164.MirrorCS", {"start": v(132.25, -7.53) * mm, "end": v(132.25, -14.53) * mm});
            skLineSegment(sketch, "E165.MirrorCS", {"start": v(134.25, -10.03) * mm, "end": v(135.75, -10.03) * mm});
            skLineSegment(sketch, "E166.MirrorCS", {"start": v(134.25, -7.53) * mm, "end": v(134.25, -10.03) * mm});
            skLineSegment(sketch, "E167.MirrorCS", {"start": v(139.25, 3.46) * mm, "end": v(136.75, 3.46) * mm});
            skLineSegment(sketch, "E168.MirrorCS", {"start": v(132.25, 5.47) * mm, "end": v(132.25, -1.53) * mm});
            skLineSegment(sketch, "E169.MirrorCS", {"start": v(134.25, 0.97) * mm, "end": v(134.25, -1.53) * mm});
            skLineSegment(sketch, "E170.MirrorCS", {"start": v(134.25, -1.53) * mm, "end": v(132.25, -1.53) * mm});
            skLineSegment(sketch, "E171.MirrorCS", {"start": v(135.75, 0.97) * mm, "end": v(134.25, 0.97) * mm});
            skLineSegment(sketch, "E172", {"start": v(132.25, -7.53) * mm, "end": v(134.25, -7.53) * mm});
            skSolve(sketch);
        }
        {
            var Q0;
            Q0=qSketchRegion(id+"F7",true);
            extrude(context, id + "F8", {"entities" : qUnion([Q0]), "depth" : 250 * mm});
        }
    });
